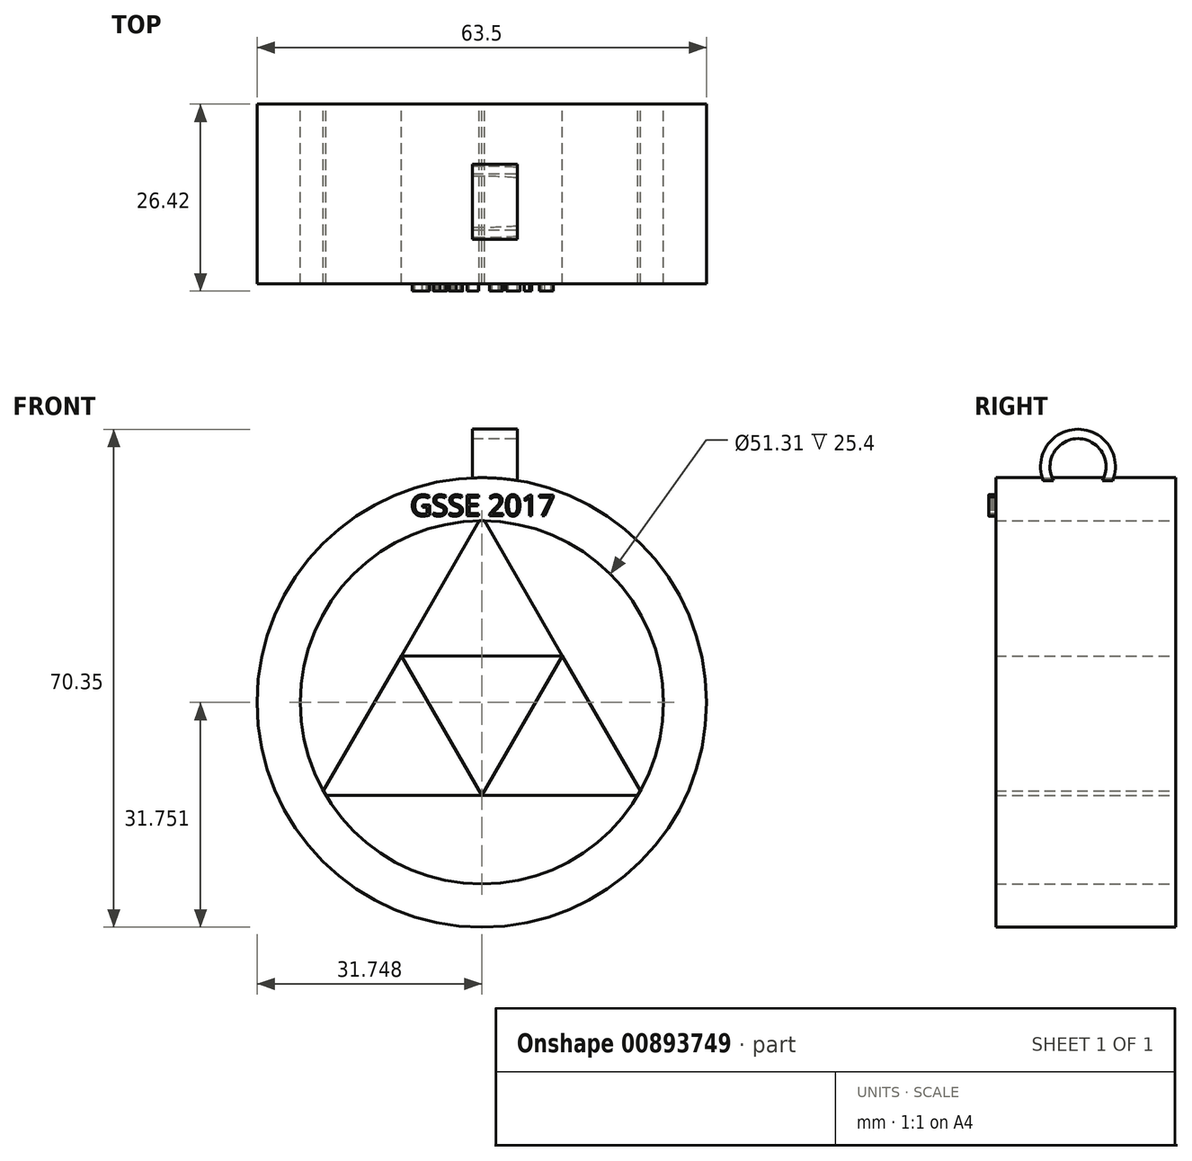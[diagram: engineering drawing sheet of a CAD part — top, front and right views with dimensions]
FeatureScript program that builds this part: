
annotation { "Feature Type Name" : "Feature", "Feature Type Description" : "" }
export const myFeature = defineFeature(function(context is Context, id is Id, definition is map)
    precondition{}
    {
        {
            var Q0;
            Q0=qCreatedBy(makeId("Front.planeOp"),FACE);
            var sketch = newSketch(context, id + "F0", { "sketchPlane" : qUnion([Q0])});
            skCircle(sketch, "E0", {"center": v(-5.02, -1.63) * mm, "radius": 31.75 * mm});
            skCircle(sketch, "E1", {"center": v(-5.02, -1.63) * mm, "radius": 25.66 * mm});
            skCircle(sketch, "E2.cCircle", {"center": v(-5.02, -1.63) * mm, "radius": 25.66 * mm, "construction": true});
            skCircle(sketch, "E3.cCircle", {"center": v(-5.02, -1.63) * mm, "radius": 26.29 * mm, "construction": true});
            skLineSegment(sketch, "E3.0", {"start": v(-4.66, 24.02) * mm, "end": v(17.38, -14.14) * mm});
            skLineSegment(sketch, "E3.1", {"start": v(17.01, -14.77) * mm, "end": v(-27.05, -14.77) * mm});
            skLineSegment(sketch, "E3.2", {"start": v(-27.42, -14.14) * mm, "end": v(-5.39, 24.02) * mm});
            skCircle(sketch, "E4.cCircle", {"center": v(-5.02, -1.63) * mm, "radius": 13.14 * mm, "construction": true});
            skLineSegment(sketch, "E4.0", {"start": v(-5.02, -14.77) * mm, "end": v(-16.4, 4.94) * mm});
            skLineSegment(sketch, "E4.1", {"start": v(-16.4, 4.94) * mm, "end": v(6.36, 4.94) * mm});
            skLineSegment(sketch, "E4.2", {"start": v(6.36, 4.94) * mm, "end": v(-5.02, -14.77) * mm});
            skPoint(sketch, "E5.orphan", {"position": v(-27.79, -14.77) * mm});
            skPoint(sketch, "E6.orphan", {"position": v(-5.02, 24.66) * mm});
            skPoint(sketch, "E7.orphan", {"position": v(17.74, -14.77) * mm});
            skSolve(sketch);
        }
        {
            var Q0;
            Q0=makeQuery(id+"F0.imprint","IMPRINT",FACE,{"disambiguationData":[TD([[makeQuery(id+"F0.imprint","IMPRINT",EDGE,{"derivedFrom":sQuery(id+"F0.wireOp",EDGE,"E0")}),1.0]])]});
            extrude(context, id + "F1", {"entities" : qUnion([Q0]), "depth" : 25.4 * mm, "offsetDistance" : 25.4 * mm});
        }
        {
            var Q0;
            {var subQ5=sQuery(id+"F0.wireOp",EDGE,"E4.1");Q0=makeQuery(id+"F0.imprint","IMPRINT",FACE,{"disambiguationData":[TD([[makeQuery(id+"F0.imprint","IMPRINT",EDGE,{"derivedFrom":subQ5}),1.0]])]});}
            var Q1;
            {var subQ5=sQuery(id+"F0.wireOp",EDGE,"E4.2");Q1=makeQuery(id+"F0.imprint","IMPRINT",FACE,{"disambiguationData":[TD([[makeQuery(id+"F0.imprint","IMPRINT",EDGE,{"derivedFrom":subQ5}),1.0]])]});}
            var Q2;
            {var subQ5=sQuery(id+"F0.wireOp",EDGE,"E4.0");Q2=makeQuery(id+"F0.imprint","IMPRINT",FACE,{"disambiguationData":[TD([[makeQuery(id+"F0.imprint","IMPRINT",EDGE,{"derivedFrom":subQ5}),1.0]])]});}
            var Q3;
            Q3=sQuery(id+"F0.wireOp",EDGE,"E3.2");
            var Q4;
            Q4=sQuery(id+"F0.wireOp",EDGE,"E3.0");
            var Q5;
            Q5=sQuery(id+"F0.wireOp",EDGE,"E3.1");
            extrude(context, id + "F2", {"entities" : qUnion([Q0, Q1, Q2]), "surfaceEntities" : qUnion([Q3, Q4, Q5]), "depth" : 25.4 * mm, "offsetDistance" : 25.4 * mm});
        }
        {
            var Q0;
            Q0=qCreatedBy(makeId("Right.planeOp"),FACE);
            var sketch = newSketch(context, id + "F3", { "sketchPlane" : qUnion([Q0])});
            skCircle(sketch, "E8", {"center": v(-13.78, 31.68) * mm, "radius": 5.3 * mm});
            skCircle(sketch, "E9", {"center": v(-13.78, 31.68) * mm, "radius": 3.96 * mm});
            skSolve(sketch);
        }
        {
            var Q0;
            Q0=makeQuery(id+"F3.imprint","IMPRINT",FACE,{"disambiguationData":[TD([[makeQuery(id+"F3.imprint","IMPRINT",EDGE,{"derivedFrom":sQuery(id+"F3.wireOp",EDGE,"E8")}),1.0]])]});
            var Q1;
            Q1=sQuery(id+"F3.wireOp",EDGE,"E8");
            extrude(context, id + "F4", {"entities" : qUnion([Q0]), "operationType" : NewBodyOperationType.ADD, "surfaceEntities" : qUnion([Q1]), "oppositeDirection" : true, "depth" : 6.35 * mm, "offsetDistance" : 25.4 * mm});
        }
        {
            var Q0;
            Q0=qCreatedBy(makeId("Front.planeOp"),FACE);
            var sketch = newSketch(context, id + "F5", { "sketchPlane" : qUnion([Q0])});
            skText(sketch, "E10", { "text": "GSSE 2017\n", "fontName": "OpenSans-Regular.ttf"});
            const initialGuessF5  = {"E10": [-0.0151, 0.02473, 1, 0, 0.00298]};
            skSetInitialGuess(sketch, initialGuessF5);
            skSolve(sketch);
        }
        {
            var Q0;
            Q0 = qSketchRegion(id + "F5", true);
            extrude(context, id + "F6", {"entities" : qUnion([Q0]), "operationType" : NewBodyOperationType.ADD, "depth" : 26.42 * mm, "offsetDistance" : 25.4 * mm});
        }
    });
